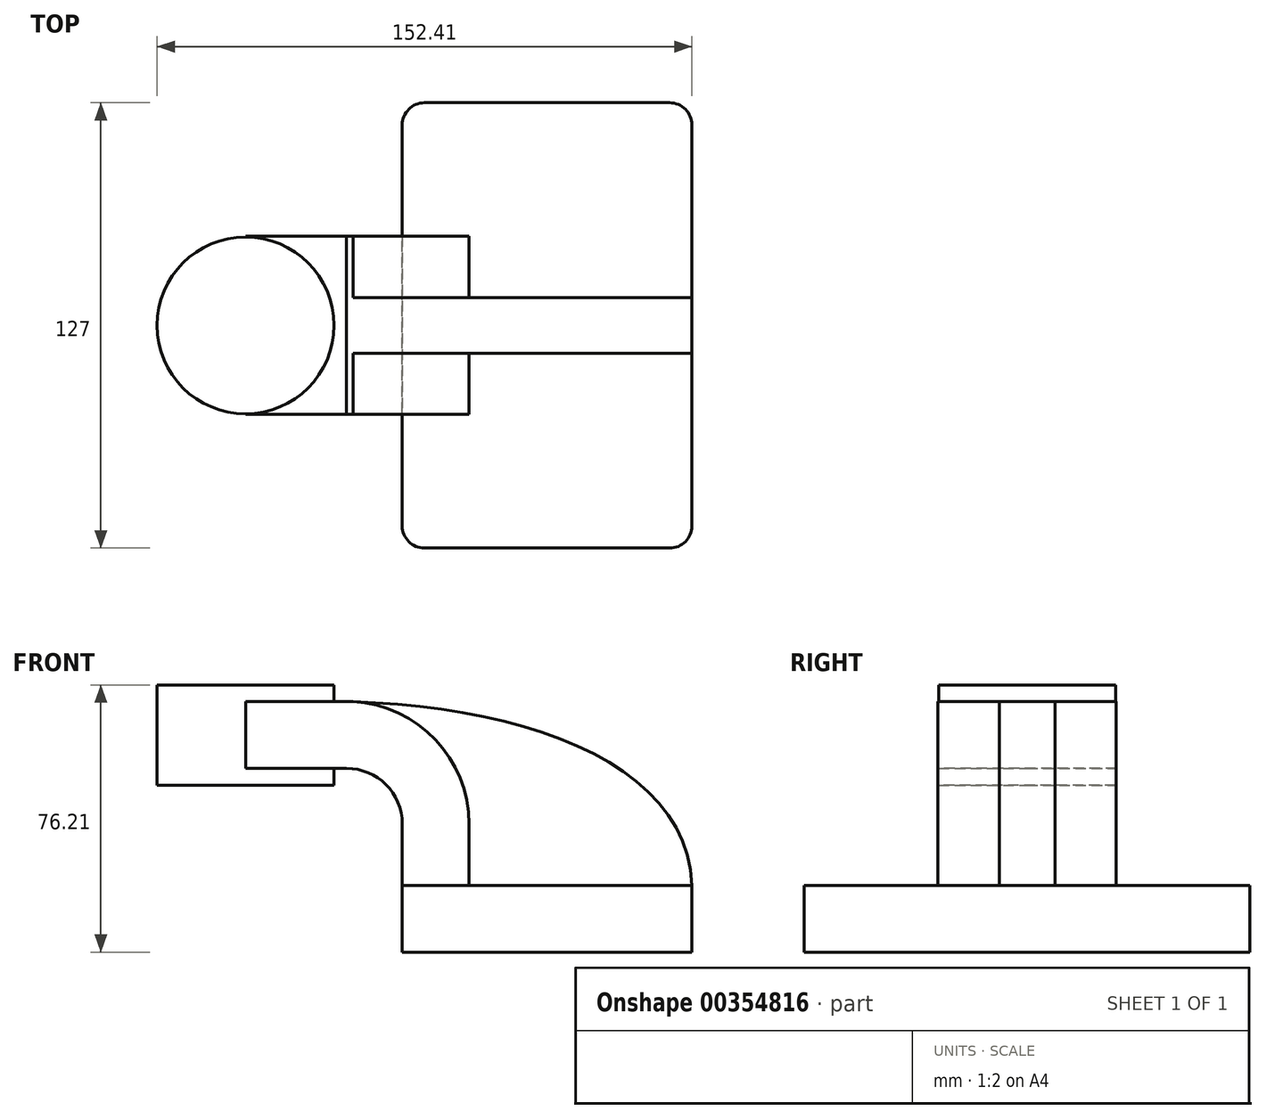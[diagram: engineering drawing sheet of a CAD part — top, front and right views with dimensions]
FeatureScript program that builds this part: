
annotation { "Feature Type Name" : "Feature", "Feature Type Description" : "" }
export const myFeature = defineFeature(function(context is Context, id is Id, definition is map)
    precondition{}
    {
        {
            var Q0;
            Q0=qCreatedBy(makeId("Front.planeOp"),FACE);
            var sketch = newSketch(context, id + "F0", { "sketchPlane" : qUnion([Q0])});
            skLineSegment(sketch, "E0.bottom", {"start": v(41.28, 9.52) * mm, "end": v(-41.28, 9.53) * mm});
            skLineSegment(sketch, "E0.top", {"start": v(41.28, -9.53) * mm, "end": v(-41.28, -9.52) * mm});
            skLineSegment(sketch, "E0.left", {"start": v(41.28, 9.52) * mm, "end": v(41.28, -9.53) * mm});
            skLineSegment(sketch, "E0.right", {"start": v(-41.28, 9.53) * mm, "end": v(-41.28, -9.52) * mm});
            skPoint(sketch, "E0.middle", {"position": v(0, 0) * mm});
            skLineSegment(sketch, "E1.bottom", {"start": v(-60.33, 38.1) * mm, "end": v(-111.13, 38.1) * mm});
            skLineSegment(sketch, "E1.top", {"start": v(-60.33, 66.68) * mm, "end": v(-111.13, 66.68) * mm});
            skLineSegment(sketch, "E1.left", {"start": v(-60.33, 38.1) * mm, "end": v(-60.33, 66.68) * mm});
            skLineSegment(sketch, "E1.right", {"start": v(-111.13, 38.1) * mm, "end": v(-111.13, 66.68) * mm});
            skPoint(sketch, "E1.middle", {"position": v(-85.73, 52.39) * mm});
            skLineSegment(sketch, "E2", {"start": v(-41.28, 9.53) * mm, "end": v(-41.28, 27) * mm});
            skArc(sketch, "E3", {"start": v(-41.28, 27) * mm, "mid": v(-45.92, 38.23) * mm, "end": v(-57.15, 42.88) * mm});
            skLineSegment(sketch, "E4", {"start": v(-57.15, 42.88) * mm, "end": v(-85.9, 42.88) * mm});
            skLineSegment(sketch, "E5.0", {"start": v(-57.15, 61.93) * mm, "end": v(-85.9, 61.93) * mm});
            skArc(sketch, "E5.1", {"start": v(-22.23, 27) * mm, "mid": v(-32.45, 51.7) * mm, "end": v(-57.15, 61.93) * mm});
            skLineSegment(sketch, "E5.2", {"start": v(-22.23, 9.53) * mm, "end": v(-22.23, 27) * mm});
            skFitSpline(sketch, "E6", {"points": [v(41.28, 9.52) * mm, v(-57.15, 61.93) * mm], "startDerivative": vector(-4.2, 105.48) * mm, "endDerivative": vector(-150.22, 3.39) * mm});
            skLineSegment(sketch, "E7", {"start": v(-85.9, 61.93) * mm, "end": v(-85.9, 42.88) * mm});
            skLineSegment(sketch, "E8", {"start": v(-85.9, 66.68) * mm, "end": v(-85.9, 38.1) * mm});
            skSolve(sketch);
        }
        {
            var Q0;
            Q0=makeQuery(id+"F0.imprint","IMPRINT",FACE,{"disambiguationData":[TD([[makeQuery(id+"F0.imprint","IMPRINT",EDGE,{"derivedFrom":sQuery(id+"F0.wireOp",EDGE,"E0.top")}),-1.0]])]});
            extrude(context, id + "F1", {"entities" : qUnion([Q0]), "endBound" : BoundingType.SYMMETRIC, "depth" : 127 * mm});
        }
        {
            var Q0;
            {var subQ1=sQuery(id+"F0.wireOp",EDGE,"E2");Q0=makeQuery(id+"F0.imprint","IMPRINT",FACE,{"disambiguationData":[TD([[makeQuery(id+"F0.imprint","IMPRINT",EDGE,{"derivedFrom":subQ1}),-1.0]])]});}
            extrude(context, id + "F2", {"entities" : qUnion([Q0]), "operationType" : NewBodyOperationType.ADD, "endBound" : BoundingType.SYMMETRIC, "oppositeDirection" : true, "depth" : 50.8 * mm});
        }
        {
            var Q0;
            {var subQ3=sQuery(id+"F0.wireOp",EDGE,"E5.2");Q0=makeQuery(id+"F0.imprint","IMPRINT",FACE,{"disambiguationData":[TD([[makeQuery(id+"F0.imprint","IMPRINT",EDGE,{"derivedFrom":subQ3}),-1.0]])]});}
            extrude(context, id + "F3", {"entities" : qUnion([Q0]), "operationType" : NewBodyOperationType.ADD, "endBound" : BoundingType.SYMMETRIC, "depth" : 15.88 * mm});
        }
        {
            var Q0;
            {var subQ0=sQuery(id+"F0.wireOp",EDGE,"E4");var subQ1=sQuery(id+"F0.wireOp",EDGE,"E1.left");var subQ2=makeQuery(id+"F0.imprint","INTERSECT",VERTEX,{"derivedFrom":[subQ1,subQ0]});Q0=makeQuery(id+"F0.imprint","IMPRINT",FACE,{"disambiguationData":[TD([[makeQuery(id+"F0.imprint","IMPRINT",EDGE,{"disambiguationData":[TD([[subQ2,-1.0]])],"derivedFrom":subQ1}),1.0]])]});}
            extrude(context, id + "F4", {"entities" : qUnion([Q0]), "operationType" : NewBodyOperationType.ADD, "endBound" : BoundingType.SYMMETRIC, "depth" : 50.8 * mm});
        }
        {
            var Q0;
            {var subQ4=sQuery(id+"F0.wireOp",EDGE,"E1.right");Q0=makeQuery(id+"F0.imprint","IMPRINT",FACE,{"disambiguationData":[TD([[makeQuery(id+"F0.imprint","IMPRINT",EDGE,{"derivedFrom":subQ4}),-1.0]])]});}
            var Q1;
            Q1=sQuery(id+"F0.wireOp",EDGE,"E8");
            revolve(context, id + "F5", {"operationType" : NewBodyOperationType.ADD, "entities" : qUnion([Q0]), "axis" : qUnion([Q1]), "revolveType" : RevolveType.FULL});
        }
        {
            var Q0;
            Q0=makeQuery(id+"F1.opExtrude","CAP_EDGE",EDGE,{"disambiguationData":[OSD([sQuery(id+"F0.wireOp",EDGE,"E0.left")])],"isStart":true});
            var Q1;
            Q1=makeQuery(id+"F1.opExtrude","CAP_EDGE",EDGE,{"disambiguationData":[OSD([sQuery(id+"F0.wireOp",EDGE,"E0.right")])],"isStart":true});
            var Q2;
            Q2=makeQuery(id+"F1.opExtrude","CAP_EDGE",EDGE,{"disambiguationData":[OSD([sQuery(id+"F0.wireOp",EDGE,"E0.right")])],"isStart":false});
            var Q3;
            Q3=makeQuery(id+"F1.opExtrude","CAP_EDGE",EDGE,{"disambiguationData":[OSD([sQuery(id+"F0.wireOp",EDGE,"E0.left")])],"isStart":false});
            fillet(context, id + "F6", {"entities" : qUnion([Q0, Q1, Q2, Q3]), "radius" : 6.35 * mm, "tangentPropagation" : true, "allowEdgeOverflow" : false});
        }
    });
